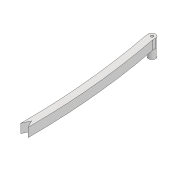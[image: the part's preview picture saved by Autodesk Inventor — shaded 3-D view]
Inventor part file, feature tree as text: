
AUTODESK INVENTOR PART (.ipt)
format: ipt  version: 2022 (Build 260153000, 153)  size: 129,024 bytes
history: native  units: mm
features: extrude x3, sketch x3, projected_geometry x2
ambient origin geometry x8: Origin, YZ Plane, XZ Plane, XY Plane, X Axis, Y Axis, Z Axis, Center Point
bodies: Solid1 (feature_tree)
feature tree (8):
  extrude  "Extrusion1"  Depth=315.198mm
  extrude  "Extrusion3"  Depth=3.0mm
  extrude  "Extrusion2"  Depth=800.0mm
  sketch  "Sketch1"  dims[d0=8.0mm d1=315.198mm]
  sketch  "Sketch3"  dims[d2=3.0mm d3=3.0mm]
  projected_geometry  "Projected Loop2"
  sketch  "Sketch4"  dims[d4=10.0mm d5=0.0mm d24=800.0mm d25=800.0mm d26=3.0mm d27=3.0mm d30=100.0mm d31=0.0mm d32=10.0mm d33=0.0mm]
  projected_geometry  "Projected Loop3"
